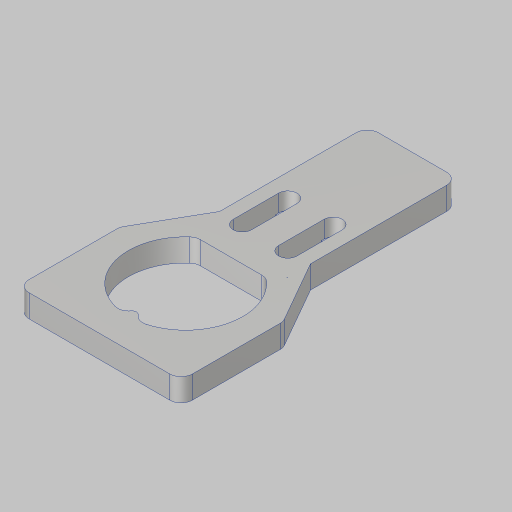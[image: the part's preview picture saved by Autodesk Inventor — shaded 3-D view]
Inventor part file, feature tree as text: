
AUTODESK INVENTOR PART (.ipt)
format: ipt  version: 2023.5 (Build 275446000, 446)  size: 310,272 bytes
history: native  units: in
note: dims shown in document units (in); Inventor stores cm internally (conversion verified against a paired STEP export)
features: extrude x7, sketch x6, fillet x5, projected_geometry x5
ambient origin geometry x8: Origin, YZ Plane, XZ Plane, XY Plane, X Axis, Y Axis, Z Axis, Center Point
bodies: Solid1 (feature_tree)
feature tree (23):
  sketch  "Sketch1"  dims[d1=0.7in d3=0.125in d4=0.197in]
  extrude  "Extrusion1"  Depth=0.125in
  fillet  "Fillet1"  Radius=0.197in
  extrude  "Extrusion2"  Depth=1.0in
  extrude  "Extrusion3"  Depth=0.25in
  fillet  "Fillet2"  Radius=0.5in
  extrude  "Extrusion4"  Depth=0.25in TaperAngle=0.0deg
  fillet  "Fillet3"  Radius=0.125in
  extrude  "Extrusion5"  Depth=0.5in
  fillet  "Fillet4"  Radius=1.375in
  extrude  "Extrusion7"  Depth=1.0in TaperAngle=0.0deg
  extrude  "Extrusion8"  Depth=0.0312in
  fillet  "Fillet5"  Radius=0.5in
  sketch  "Sketch2"  dims[d5=0.197in d8=1.0in]
  sketch  "Sketch3"  dims[d9=2.0in d10=0.25in d11=0.5in]
  sketch  "Sketch4"  dims[d12=0.25in d13=0.25in d14=0.0in d22=0.125in]
  sketch  "Sketch5"  dims[d23=0.201in d24=0.5in d26=1.375in]
  sketch  "Sketch7"  dims[d27=0.5in d28=1.0in d29=0.0in d30=1.26in d31=0.5in d32=0.125in d33=1.0in d34=0.0in d35=0.125in d36=0.093in d37=0.042in d38=1.0in d39=0.0in d40=0.125in d41=0.7874in d43=0.197in d44=0.3937in d46=1.0in d48=1.8in d49=3.45in d50=1.125in d51=1.0in d52=0.0in d53=0.125in d58=0.17in d59=0.0in d61=0.06in d62=0.0in d63=0.0312in]
  projected_geometry  "Project Cut Edges1"
  projected_geometry  "Project Cut Edges2"
  projected_geometry  "Project Cut Edges3"
  projected_geometry  "Project Cut Edges4"
  projected_geometry  "Project Cut Edges5"
